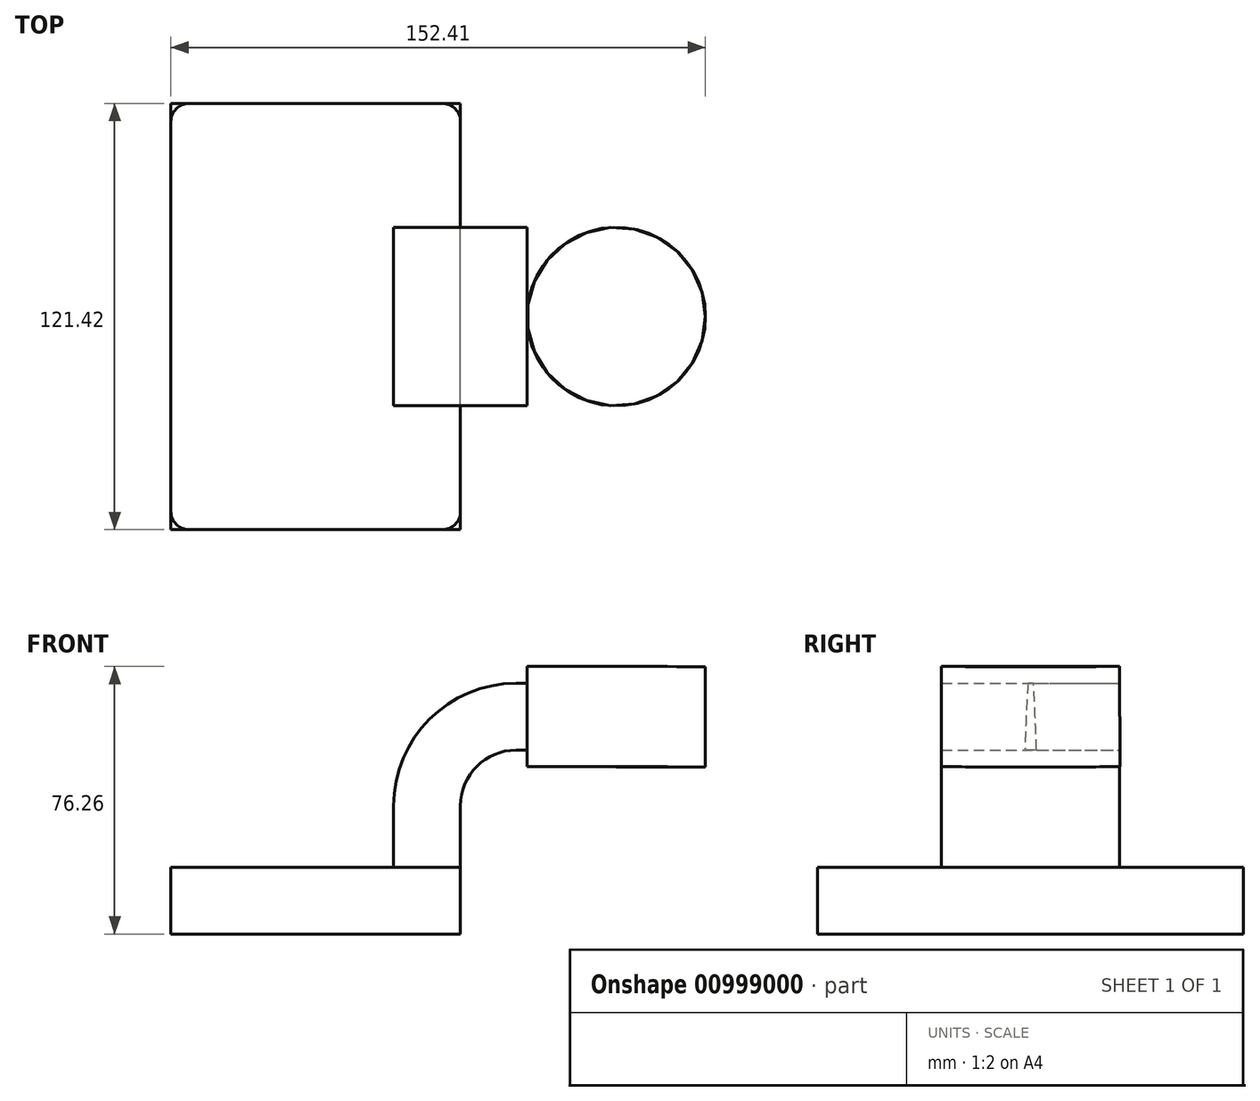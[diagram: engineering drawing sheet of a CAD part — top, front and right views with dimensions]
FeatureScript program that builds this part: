
annotation { "Feature Type Name" : "Feature", "Feature Type Description" : "" }
export const myFeature = defineFeature(function(context is Context, id is Id, definition is map)
    precondition{}
    {
        {
            var Q0;
            Q0=qCreatedBy(makeId("Front.planeOp"),FACE);
            var sketch = newSketch(context, id + "F0", { "sketchPlane" : qUnion([Q0])});
            skLineSegment(sketch, "E0.bottom", {"start": v(-41.28, -9.52) * mm, "end": v(41.28, -9.52) * mm});
            skLineSegment(sketch, "E0.top", {"start": v(-41.28, 9.53) * mm, "end": v(41.27, 9.53) * mm});
            skLineSegment(sketch, "E0.left", {"start": v(-41.28, -9.52) * mm, "end": v(-41.28, 9.53) * mm});
            skLineSegment(sketch, "E0.right", {"start": v(41.28, -9.52) * mm, "end": v(41.28, 9.53) * mm});
            skPoint(sketch, "E0.middle", {"position": v(0, 0) * mm});
            skLineSegment(sketch, "E1.bottom", {"start": v(60.33, 38.1) * mm, "end": v(111.13, 38.1) * mm});
            skLineSegment(sketch, "E1.top", {"start": v(60.33, 66.67) * mm, "end": v(111.13, 66.67) * mm});
            skLineSegment(sketch, "E1.left", {"start": v(60.33, 38.1) * mm, "end": v(60.33, 66.68) * mm});
            skLineSegment(sketch, "E1.right", {"start": v(111.13, 38.1) * mm, "end": v(111.13, 66.68) * mm});
            skPoint(sketch, "E1.middle", {"position": v(85.73, 52.39) * mm});
            skLineSegment(sketch, "E2", {"start": v(41.27, 9.53) * mm, "end": v(41.27, 27) * mm});
            skArc(sketch, "E3", {"start": v(41.27, 27) * mm, "mid": v(45.92, 38.23) * mm, "end": v(57.15, 42.88) * mm});
            skLineSegment(sketch, "E4", {"start": v(57.15, 42.88) * mm, "end": v(85.7, 42.88) * mm});
            skLineSegment(sketch, "E5.0", {"start": v(57.15, 61.93) * mm, "end": v(86.02, 61.93) * mm});
            skArc(sketch, "E5.1", {"start": v(22.23, 27) * mm, "mid": v(32.45, 51.7) * mm, "end": v(57.15, 61.93) * mm});
            skLineSegment(sketch, "E5.2", {"start": v(22.23, 8.52) * mm, "end": v(22.23, 27) * mm});
            skLineSegment(sketch, "E6", {"start": v(85.73, 66.67) * mm, "end": v(85.7, 38.1) * mm});
            skPoint(sketch, "E6.endSnap0", {"position": v(85.73, 38.1) * mm});
            skPoint(sketch, "E7.1.internal.snap0", {"position": v(32.45, 51.7) * mm});
            skFitSpline(sketch, "E8", {"points": [v(-41.28, 9.53) * mm, v(57.15, 61.93) * mm], "startDerivative": vector(4.96, 106.3) * mm, "endDerivative": vector(111.4, -12.02) * mm});
            skSolve(sketch);
        }
        {
            var Q0;
            Q0=makeQuery(id+"F0.imprint","IMPRINT",FACE,{"disambiguationData":[TD([[makeQuery(id+"F0.imprint","IMPRINT",EDGE,{"derivedFrom":sQuery(id+"F0.wireOp",EDGE,"E0.bottom")}),1.0]])]});
            var sketch = newSketch(context, id + "F1", { "sketchPlane" : qUnion([Q0])});
            skSolve(sketch);
        }
        {
            var Q0;
            Q0=makeQuery(id+"F0.imprint","IMPRINT",FACE,{"disambiguationData":[TD([[makeQuery(id+"F0.imprint","IMPRINT",EDGE,{"derivedFrom":sQuery(id+"F0.wireOp",EDGE,"E0.bottom")}),1.0]])]});
            var sketch = newSketch(context, id + "F2", { "sketchPlane" : qUnion([Q0])});
            skSolve(sketch);
        }
        {
            var Q0;
            Q0=makeQuery(id+"F0.imprint","IMPRINT",FACE,{"disambiguationData":[TD([[makeQuery(id+"F0.imprint","IMPRINT",EDGE,{"derivedFrom":sQuery(id+"F0.wireOp",EDGE,"E0.bottom")}),1.0]])]});
            var Q1;
            Q1=makeQuery(id+"F1.imprint","IMPRINT",FACE,{"disambiguationData":[TD([[makeQuery(id+"F1.imprint","IMPRINT",EDGE,{"derivedFrom":makeQuery(id+"F0.imprint","IMPRINT",EDGE,{"derivedFrom":sQuery(id+"F0.wireOp",EDGE,"E0.bottom")})}),1.0]])]});
            var Q2;
            Q2=makeQuery(id+"F2.imprint","IMPRINT",FACE,{"disambiguationData":[TD([[makeQuery(id+"F2.imprint","IMPRINT",EDGE,{"derivedFrom":makeQuery(id+"F0.imprint","IMPRINT",EDGE,{"derivedFrom":sQuery(id+"F0.wireOp",EDGE,"E0.bottom")})}),1.0]])]});
            extrude(context, id + "F3", {"entities" : qUnion([Q0, Q1, Q2]), "endBound" : BoundingType.SYMMETRIC, "depth" : 121.4 * mm, "offsetDistance" : 25.4 * mm});
        }
        {
            var Q0;
            {var subQ4=sQuery(id+"F0.wireOp",EDGE,"E5.1");Q0=makeQuery(id+"F0.imprint","IMPRINT",FACE,{"disambiguationData":[TD([[makeQuery(id+"F0.imprint","IMPRINT",EDGE,{"derivedFrom":subQ4}),1.0]])]});}
            var Q1;
            {var subQ1=sQuery(id+"F0.wireOp",EDGE,"E2");Q1=makeQuery(id+"F0.imprint","IMPRINT",FACE,{"disambiguationData":[TD([[makeQuery(id+"F0.imprint","IMPRINT",EDGE,{"derivedFrom":subQ1}),1.0]])]});}
            extrude(context, id + "F4", {"entities" : qUnion([Q0, Q1]), "endBound" : BoundingType.SYMMETRIC, "depth" : 50.8 * mm, "offsetDistance" : 25.4 * mm});
        }
        {
            var Q0;
            {var subQ4=sQuery(id+"F0.wireOp",EDGE,"E1.right");Q0=makeQuery(id+"F0.imprint","IMPRINT",FACE,{"disambiguationData":[TD([[makeQuery(id+"F0.imprint","IMPRINT",EDGE,{"derivedFrom":subQ4}),1.0]])]});}
            var Q1;
            Q1=sQuery(id+"F0.wireOp",EDGE,"E6");
            revolve(context, id + "F5", {"operationType" : NewBodyOperationType.ADD, "surfaceOperationType" : NewSurfaceOperationType.NEW, "entities" : qUnion([Q0]), "axis" : qUnion([Q1]), "revolveType" : RevolveType.FULL});
        }
        {
            var Q0;
            {var subQ0=sQuery(id+"F0.wireOp",EDGE,"E0.left");Q0=makeQuery(id+"F3.opExtrude","CAP_EDGE",EDGE,{"disambiguationData":[OSD([subQ0]),TDD([makeQuery(id+"F0.imprint","IMPRINT",EDGE,{"derivedFrom":subQ0})])],"isStart":false});}
            var Q1;
            {var subQ0=sQuery(id+"F0.wireOp",EDGE,"E0.right");Q1=makeQuery(id+"F3.opExtrude","CAP_EDGE",EDGE,{"disambiguationData":[OSD([subQ0]),TDD([makeQuery(id+"F0.imprint","IMPRINT",EDGE,{"derivedFrom":subQ0})])],"isStart":false});}
            var Q2;
            {var subQ0=sQuery(id+"F0.wireOp",EDGE,"E0.right");Q2=makeQuery(id+"F3.opExtrude","CAP_EDGE",EDGE,{"disambiguationData":[OSD([subQ0]),TDD([makeQuery(id+"F0.imprint","IMPRINT",EDGE,{"derivedFrom":subQ0})])],"isStart":true});}
            var Q3;
            {var subQ0=sQuery(id+"F0.wireOp",EDGE,"E0.left");Q3=makeQuery(id+"F3.opExtrude","CAP_EDGE",EDGE,{"disambiguationData":[OSD([subQ0]),TDD([makeQuery(id+"F0.imprint","IMPRINT",EDGE,{"derivedFrom":subQ0})])],"isStart":true});}
            fillet(context, id + "F6", {"entities" : qUnion([Q0, Q1, Q2, Q3]), "radius" : 5.08 * mm, "tangentPropagation" : true, "allowEdgeOverflow" : false});
        }
    });
